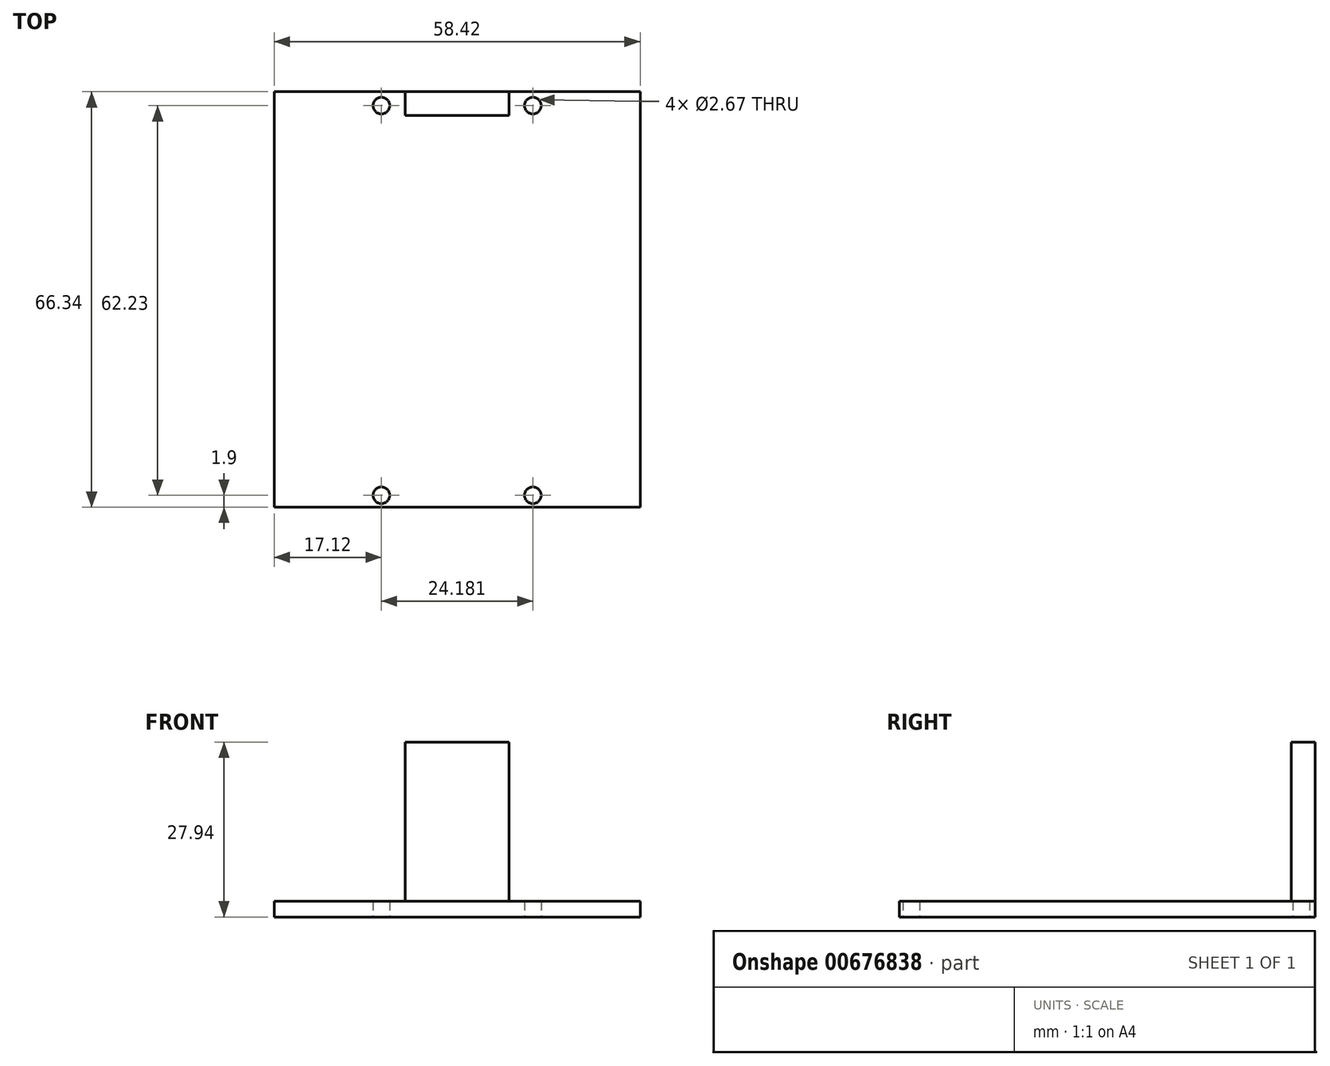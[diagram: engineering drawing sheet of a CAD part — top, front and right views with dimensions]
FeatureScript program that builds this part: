
annotation { "Feature Type Name" : "Feature", "Feature Type Description" : "" }
export const myFeature = defineFeature(function(context is Context, id is Id, definition is map)
    precondition{}
    {
        {
            var Q0;
            Q0=qCreatedBy(makeId("Top.planeOp"),FACE);
            var sketch = newSketch(context, id + "F0", { "sketchPlane" : qUnion([Q0])});
            skLineSegment(sketch, "E0.bottom", {"start": v(0, 0) * mm, "end": v(58.42, 0) * mm});
            skLineSegment(sketch, "E0.top", {"start": v(0, -66.34) * mm, "end": v(58.42, -66.34) * mm});
            skLineSegment(sketch, "E0.left", {"start": v(0, 0) * mm, "end": v(0, -66.34) * mm});
            skLineSegment(sketch, "E0.right", {"start": v(58.42, 0) * mm, "end": v(58.42, -66.34) * mm});
            skCircle(sketch, "E1", {"center": v(41.3, -64.44) * mm, "radius": 1.33 * mm});
            skCircle(sketch, "E2", {"center": v(17.12, -64.44) * mm, "radius": 1.33 * mm});
            skCircle(sketch, "E3", {"center": v(41.3, -2.2) * mm, "radius": 1.33 * mm});
            skCircle(sketch, "E4", {"center": v(17.12, -2.2) * mm, "radius": 1.33 * mm});
            skSolve(sketch);
        }
        {
            var Q0;
            Q0=makeQuery(id+"F0.imprint","IMPRINT",FACE,{"disambiguationData":[TD([[makeQuery(id+"F0.imprint","IMPRINT",EDGE,{"derivedFrom":sQuery(id+"F0.wireOp",EDGE,"E0.bottom")}),-1.0]])]});
            extrude(context, id + "F1", {"entities" : qUnion([Q0]), "depth" : 2.54 * mm, "offsetDistance" : 25.4 * mm});
        }
        {
            var Q0;
            Q0=makeQuery(id+"F1.opExtrude","CAP_FACE",FACE,{"disambiguationData":[OSD([sQuery(id+"F0.wireOp",EDGE,"E0.bottom"),sQuery(id+"F0.wireOp",EDGE,"E0.top"),sQuery(id+"F0.wireOp",EDGE,"E0.left"),sQuery(id+"F0.wireOp",EDGE,"E0.right"),sQuery(id+"F0.wireOp",EDGE,"E1"),sQuery(id+"F0.wireOp",EDGE,"E2"),sQuery(id+"F0.wireOp",EDGE,"E3"),sQuery(id+"F0.wireOp",EDGE,"E4")])],"isStart":false});
            var sketch = newSketch(context, id + "F2", { "sketchPlane" : qUnion([Q0])});
            skLineSegment(sketch, "E5.bottom", {"start": v(37.46, -3.8) * mm, "end": v(20.96, -3.81) * mm});
            skLineSegment(sketch, "E5.top", {"start": v(37.46, 0) * mm, "end": v(20.96, 0) * mm});
            skLineSegment(sketch, "E5.left", {"start": v(37.46, -3.8) * mm, "end": v(37.46, 0) * mm});
            skLineSegment(sketch, "E5.right", {"start": v(20.96, -3.81) * mm, "end": v(20.96, 0) * mm});
            skSolve(sketch);
        }
        {
            var Q0;
            Q0=makeQuery(id+"F2.imprint","IMPRINT",FACE,{"disambiguationData":[TD([[makeQuery(id+"F2.imprint","IMPRINT",EDGE,{"derivedFrom":sQuery(id+"F2.wireOp",EDGE,"E5.bottom")}),-1.0]])]});
            extrude(context, id + "F3", {"entities" : qUnion([Q0]), "operationType" : NewBodyOperationType.ADD, "depth" : 25.4 * mm, "offsetDistance" : 25.4 * mm});
        }
    });
